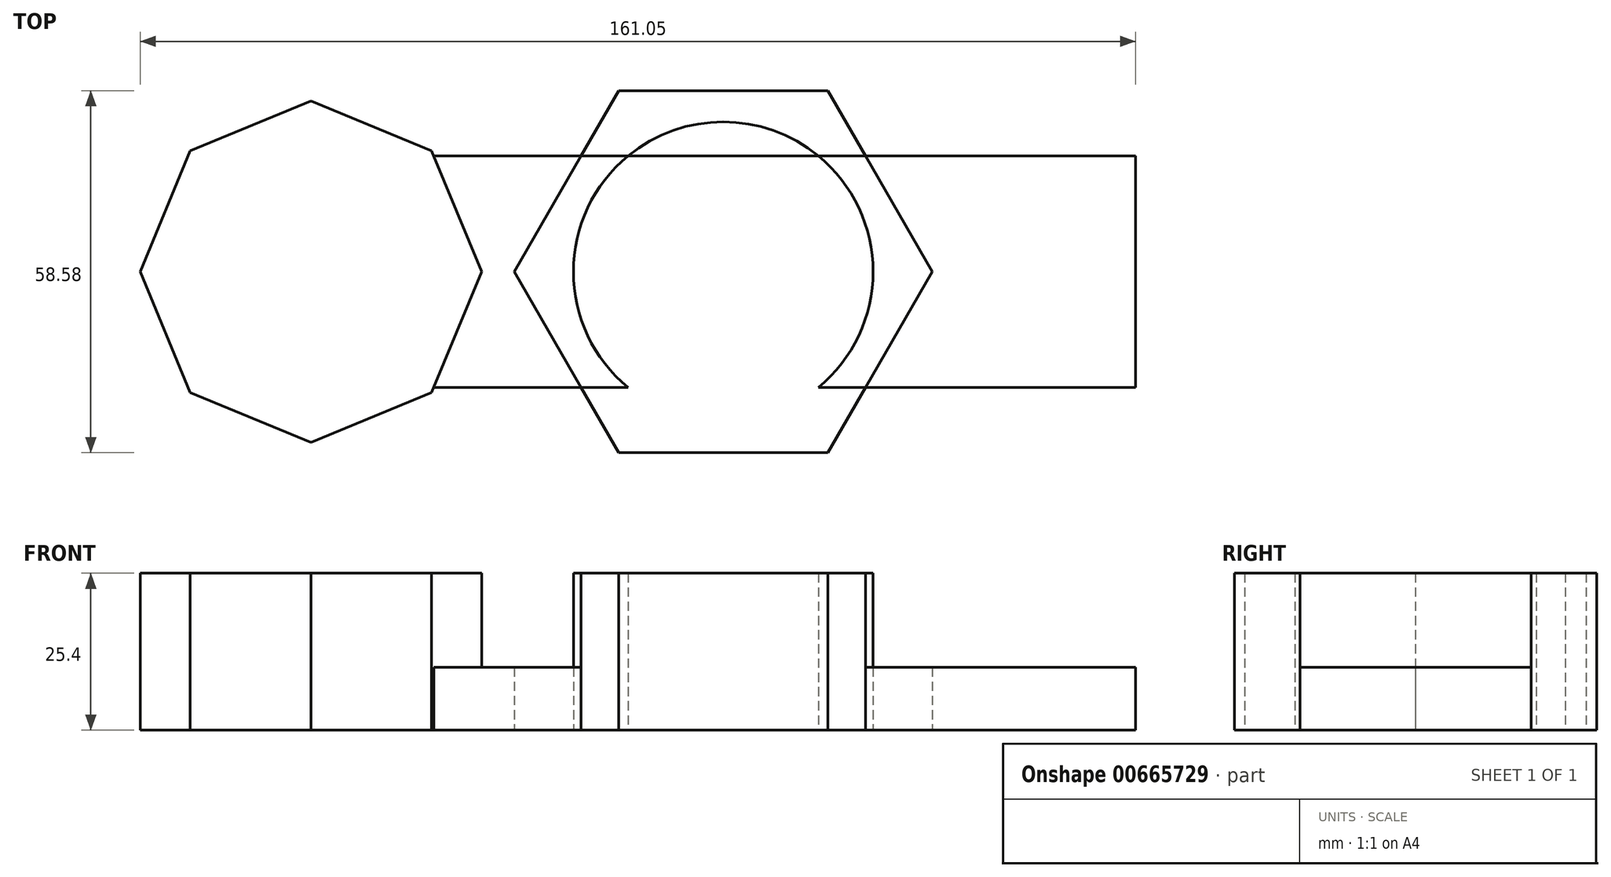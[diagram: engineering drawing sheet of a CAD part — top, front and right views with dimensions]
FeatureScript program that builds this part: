
annotation { "Feature Type Name" : "Feature", "Feature Type Description" : "" }
export const myFeature = defineFeature(function(context is Context, id is Id, definition is map)
    precondition{}
    {
        {
            var Q0;
            Q0=qCreatedBy(makeId("Top.planeOp"),FACE);
            var sketch = newSketch(context, id + "F0", { "sketchPlane" : qUnion([Q0])});
            skCircle(sketch, "E0", {"center": v(0, 0) * mm, "radius": 24.25 * mm});
            skLineSegment(sketch, "E1.0", {"start": v(16.91, -29.3) * mm, "end": v(-16.91, -29.3) * mm});
            skLineSegment(sketch, "E1.1", {"start": v(-16.91, -29.3) * mm, "end": v(-33.83, 0) * mm});
            skLineSegment(sketch, "E1.2", {"start": v(-33.83, 0) * mm, "end": v(-16.91, 29.3) * mm});
            skLineSegment(sketch, "E1.3", {"start": v(-16.91, 29.3) * mm, "end": v(16.91, 29.3) * mm});
            skLineSegment(sketch, "E1.4", {"start": v(16.91, 29.3) * mm, "end": v(33.83, 0) * mm});
            skLineSegment(sketch, "E1.5", {"start": v(33.83, 0) * mm, "end": v(16.91, -29.3) * mm});
            skPoint(sketch, "E1.0.midPoint", {"position": v(0, -29.3) * mm});
            skLineSegment(sketch, "E2.bottom", {"start": v(66.72, -18.71) * mm, "end": v(-46.85, -18.71) * mm});
            skLineSegment(sketch, "E2.top", {"start": v(66.72, 18.71) * mm, "end": v(-46.85, 18.71) * mm});
            skLineSegment(sketch, "E2.left", {"start": v(66.72, -18.71) * mm, "end": v(66.72, 18.71) * mm});
            skArc(sketch, "E3", {"start": v(66.72, -18.71) * mm, "mid": v(85.43, 0) * mm, "end": v(66.72, 18.71) * mm});
            skLineSegment(sketch, "E4.0", {"start": v(-39.1, 0) * mm, "end": v(-47.2, -19.53) * mm});
            skLineSegment(sketch, "E4.1", {"start": v(-47.2, -19.53) * mm, "end": v(-66.72, -27.62) * mm});
            skLineSegment(sketch, "E4.2", {"start": v(-66.72, -27.62) * mm, "end": v(-86.25, -19.53) * mm});
            skLineSegment(sketch, "E4.3", {"start": v(-86.25, -19.53) * mm, "end": v(-94.33, 0) * mm});
            skLineSegment(sketch, "E4.4", {"start": v(-94.33, 0) * mm, "end": v(-86.25, 19.53) * mm});
            skLineSegment(sketch, "E4.5", {"start": v(-86.25, 19.53) * mm, "end": v(-66.72, 27.62) * mm});
            skLineSegment(sketch, "E4.6", {"start": v(-66.72, 27.62) * mm, "end": v(-47.2, 19.53) * mm});
            skLineSegment(sketch, "E4.7", {"start": v(-47.2, 19.53) * mm, "end": v(-39.1, 0) * mm});
            skPoint(sketch, "E5.orphan", {"position": v(-66.72, 18.71) * mm});
            skPoint(sketch, "E6.orphan", {"position": v(-66.72, -18.71) * mm});
            skLineSegment(sketch, "E7", {"start": v(-14.07, 0) * mm, "end": v(-94.08, 0) * mm});
            skLineSegment(sketch, "E8", {"start": v(-15.53, 0) * mm, "end": v(-143.06, 0) * mm});
            skSolve(sketch);
        }
        {
            var Q0;
            {var subQ3=sQuery(id+"F0.wireOp",EDGE,"E2.bottom");var subQ5=sQuery(id+"F0.wireOp",EDGE,"E4.0");var subQ6=makeQuery(id+"F0.imprint","INTERSECT",VERTEX,{"derivedFrom":[subQ3,subQ5]});Q0=makeQuery(id+"F0.imprint","IMPRINT",FACE,{"disambiguationData":[TD([[makeQuery(id+"F0.imprint","IMPRINT",EDGE,{"disambiguationData":[TD([[subQ6,1.0]])],"derivedFrom":subQ3}),-1.0]])]});}
            var Q1;
            {var subQ3=sQuery(id+"F0.wireOp",EDGE,"E2.top");var subQ5=sQuery(id+"F0.wireOp",EDGE,"E4.7");var subQ7=makeQuery(id+"F0.imprint","INTERSECT",VERTEX,{"derivedFrom":[subQ3,subQ5]});Q1=makeQuery(id+"F0.imprint","IMPRINT",FACE,{"disambiguationData":[TD([[makeQuery(id+"F0.imprint","IMPRINT",EDGE,{"disambiguationData":[TD([[subQ7,1.0]])],"derivedFrom":subQ3}),1.0]])]});}
            var Q2;
            {var subQ1=sQuery(id+"F0.wireOp",EDGE,"E2.left");Q2=makeQuery(id+"F0.imprint","IMPRINT",FACE,{"disambiguationData":[TD([[makeQuery(id+"F0.imprint","IMPRINT",EDGE,{"derivedFrom":subQ1}),1.0]])]});}
            extrude(context, id + "F1", {"entities" : qUnion([Q0, Q1, Q2]), "depth" : 10.16 * mm, "offsetDistance" : 25.4 * mm});
        }
        {
            var Q0;
            {var subQ0=sQuery(id+"F0.wireOp",EDGE,"E4.1");Q0=makeQuery(id+"F0.imprint","IMPRINT",FACE,{"disambiguationData":[TD([[makeQuery(id+"F0.imprint","IMPRINT",EDGE,{"derivedFrom":subQ0}),-1.0]])]});}
            var Q1;
            {var subQ3=sQuery(id+"F0.wireOp",EDGE,"E4.4");Q1=makeQuery(id+"F0.imprint","IMPRINT",FACE,{"disambiguationData":[TD([[makeQuery(id+"F0.imprint","IMPRINT",EDGE,{"derivedFrom":subQ3}),-1.0]])]});}
            var Q2;
            {var subQ1=sQuery(id+"F0.wireOp",EDGE,"E0");var subQ6=makeQuery(id+"F0.imprint","INTERSECT",VERTEX,{"derivedFrom":[subQ1,sQuery(id+"F0.wireOp",EDGE,"E8")]});Q2=makeQuery(id+"F0.imprint","IMPRINT",FACE,{"disambiguationData":[TD([[makeQuery(id+"F0.imprint","IMPRINT",EDGE,{"disambiguationData":[TD([[subQ6,1.0]])],"derivedFrom":subQ1}),1.0]])]});}
            var Q3;
            {var subQ0=sQuery(id+"F0.wireOp",EDGE,"E2.bottom");var subQ1=sQuery(id+"F0.wireOp",EDGE,"E0");var subQ2=makeQuery(id+"F0.imprint","INTERSECT",VERTEX,{"disambiguationData":[OD(0.0)],"derivedFrom":[subQ1,subQ0]});Q3=makeQuery(id+"F0.imprint","IMPRINT",FACE,{"disambiguationData":[TD([[makeQuery(id+"F0.imprint","IMPRINT",EDGE,{"disambiguationData":[TD([[subQ2,-1.0]])],"derivedFrom":subQ1}),1.0]])]});}
            var Q4;
            {var subQ1=sQuery(id+"F0.wireOp",EDGE,"E1.0");Q4=makeQuery(id+"F0.imprint","IMPRINT",FACE,{"disambiguationData":[TD([[makeQuery(id+"F0.imprint","IMPRINT",EDGE,{"derivedFrom":subQ1}),-1.0]])]});}
            var Q5;
            {var subQ1=sQuery(id+"F0.wireOp",EDGE,"E1.3");Q5=makeQuery(id+"F0.imprint","IMPRINT",FACE,{"disambiguationData":[TD([[makeQuery(id+"F0.imprint","IMPRINT",EDGE,{"derivedFrom":subQ1}),-1.0]])]});}
            extrude(context, id + "F2", {"entities" : qUnion([Q0, Q1, Q2, Q3, Q4, Q5]), "operationType" : NewBodyOperationType.ADD, "depth" : 25.4 * mm, "offsetDistance" : 25.4 * mm});
        }
    });
